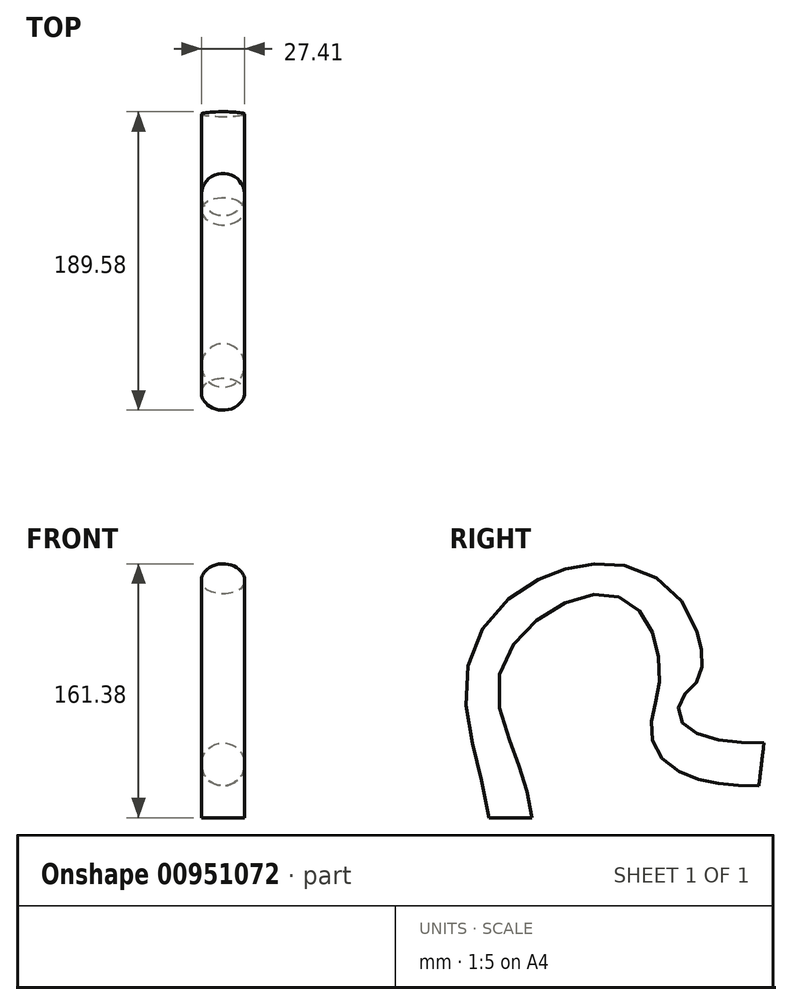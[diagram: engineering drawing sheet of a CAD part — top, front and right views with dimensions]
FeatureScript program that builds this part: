
annotation { "Feature Type Name" : "Feature", "Feature Type Description" : "" }
export const myFeature = defineFeature(function(context is Context, id is Id, definition is map)
    precondition{}
    {
        {
            var Q0;
            Q0=qCreatedBy(makeId("Top.planeOp"),FACE);
            var sketch = newSketch(context, id + "F0", { "sketchPlane" : qUnion([Q0])});
            skCircle(sketch, "E0", {"center": v(-19.75, 65.19) * mm, "radius": 13.7 * mm});
            skSolve(sketch);
        }
        {
            var Q0;
            Q0=qCreatedBy(makeId("Right.planeOp"),FACE);
            var sketch = newSketch(context, id + "F1", { "sketchPlane" : qUnion([Q0])});
            skFitSpline(sketch, "E1", {"points": [v(85.68, 40.2) * mm, v(92.25, 101.53) * mm, v(139.37, 107.34) * mm, v(170.41, 30.7) * mm, v(262.14, 8.88) * mm], "startDerivative": vector(-39.31, 304.25) * mm, "endDerivative": vector(386.74, 3.72) * mm});
            skSolve(sketch);
        }
        {
            var Q0;
            Q0=makeQuery(id+"F0.imprint","IMPRINT",FACE,{"disambiguationData":[TD([[makeQuery(id+"F0.imprint","IMPRINT",EDGE,{"derivedFrom":sQuery(id+"F0.wireOp",EDGE,"E0")}),1.0]])]});
            var Q1;
            Q1=sQuery(id+"F1.wireOp",EDGE,"E1");
            sweep(context, id + "F2", {"profiles" : qUnion([Q0]), "path" : qUnion([Q1])});
        }
    });
